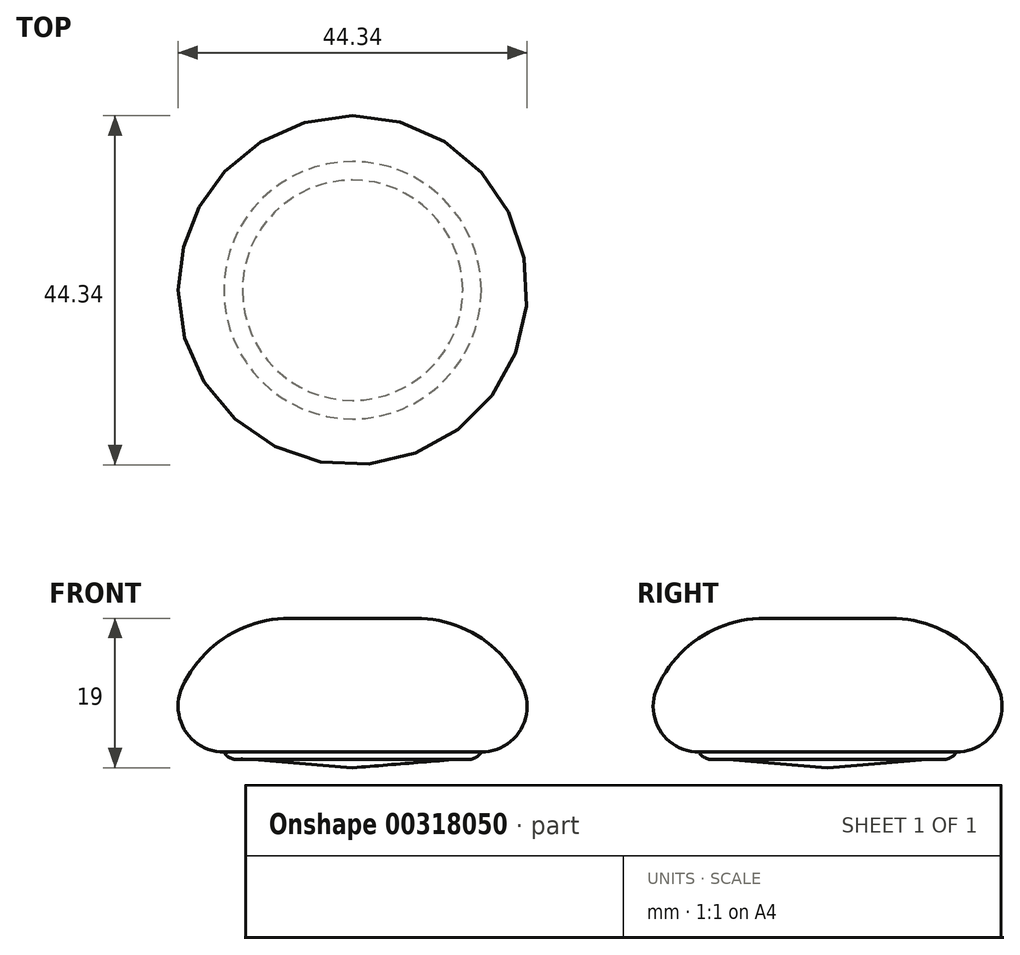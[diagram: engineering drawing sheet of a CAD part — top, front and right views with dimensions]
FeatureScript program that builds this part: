
annotation { "Feature Type Name" : "Feature", "Feature Type Description" : "" }
export const myFeature = defineFeature(function(context is Context, id is Id, definition is map)
    precondition{}
    {
        {
            var Q0;
            Q0=qCreatedBy(makeId("Front.planeOp"),FACE);
            var sketch = newSketch(context, id + "F0", { "sketchPlane" : qUnion([Q0])});
            skLineSegment(sketch, "E0", {"start": v(0, 0) * mm, "end": v(8, 0) * mm});
            skArc(sketch, "E1", {"start": v(21.64, -8.76) * mm, "mid": v(16.1, -2.38) * mm, "end": v(8, 0) * mm});
            skLineSegment(sketch, "E2", {"start": v(0, -17) * mm, "end": v(0, 0) * mm});
            skArc(sketch, "E3", {"start": v(14, -17.85) * mm, "mid": v(15.32, -17.84) * mm, "end": v(16.35, -17) * mm});
            skLineSegment(sketch, "E4", {"start": v(16.35, -17) * mm, "end": v(0, -17) * mm, "construction": true});
            skArc(sketch, "E5", {"start": v(16.35, -17) * mm, "mid": v(21.25, -14.33) * mm, "end": v(21.64, -8.76) * mm});
            skLineSegment(sketch, "E6", {"start": v(14, -17.85) * mm, "end": v(0, -19) * mm});
            skLineSegment(sketch, "E7", {"start": v(0, -19) * mm, "end": v(0, -17) * mm});
            skSolve(sketch);
        }
        {
            var Q0;
            Q0=makeQuery(id+"F0.imprint","IMPRINT",FACE,{"disambiguationData":[TD([[makeQuery(id+"F0.imprint","IMPRINT",EDGE,{"derivedFrom":sQuery(id+"F0.wireOp",EDGE,"E0")}),-1.0]])]});
            var Q1;
            Q1=sQuery(id+"F0.wireOp",EDGE,"E2");
            revolve(context, id + "F1", {"entities" : qUnion([Q0]), "axis" : qUnion([Q1]), "revolveType" : RevolveType.FULL});
        }
    });
